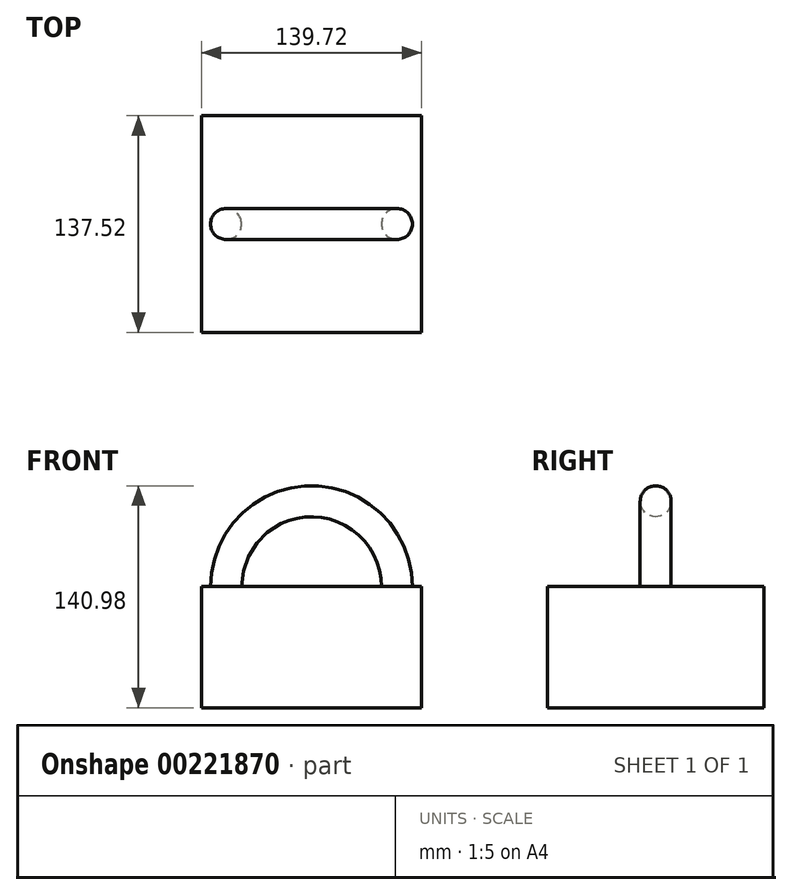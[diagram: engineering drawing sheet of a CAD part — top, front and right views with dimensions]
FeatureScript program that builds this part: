
annotation { "Feature Type Name" : "Feature", "Feature Type Description" : "" }
export const myFeature = defineFeature(function(context is Context, id is Id, definition is map)
    precondition{}
    {
        {
            var Q0;
            Q0=qCreatedBy(makeId("Top.planeOp"),FACE);
            var sketch = newSketch(context, id + "F0", { "sketchPlane" : qUnion([Q0])});
            skLineSegment(sketch, "E0.bottom", {"start": v(69.86, -68.76) * mm, "end": v(-69.86, -68.76) * mm});
            skLineSegment(sketch, "E0.top", {"start": v(69.86, 68.76) * mm, "end": v(-69.86, 68.76) * mm});
            skLineSegment(sketch, "E0.left", {"start": v(69.86, -68.76) * mm, "end": v(69.86, 68.76) * mm});
            skLineSegment(sketch, "E0.right", {"start": v(-69.86, -68.76) * mm, "end": v(-69.86, 68.76) * mm});
            skPoint(sketch, "E0.middle", {"position": v(0, 0) * mm});
            skLineSegment(sketch, "E1", {"start": v(0, 68.76) * mm, "end": v(0, -68.76) * mm});
            skSolve(sketch);
        }
        {
            var Q0;
            Q0=qCreatedBy(makeId("Top.planeOp"),FACE);
            var sketch = newSketch(context, id + "F1", { "sketchPlane" : qUnion([Q0])});
            skCircle(sketch, "E2", {"center": v(54.26, 0) * mm, "radius": 9.82 * mm});
            skSolve(sketch);
        }
        {
            var Q0;
            Q0=makeQuery(id+"F1.imprint","IMPRINT",FACE,{"disambiguationData":[TD([[makeQuery(id+"F1.imprint","IMPRINT",EDGE,{"derivedFrom":sQuery(id+"F1.wireOp",EDGE,"E2")}),1.0]])]});
            var Q1;
            Q1=sQuery(id+"F0.wireOp",EDGE,"E1");
            revolve(context, id + "F2", {"entities" : qUnion([Q0]), "axis" : qUnion([Q1]), "revolveType" : RevolveType.FULL});
        }
        {
            var Q0;
            Q0 = qSketchRegion(id + "F0", true);
            extrude(context, id + "F3", {"entities" : qUnion([Q0]), "operationType" : NewBodyOperationType.ADD, "oppositeDirection" : true, "depth" : 76.89 * mm});
        }
    });
